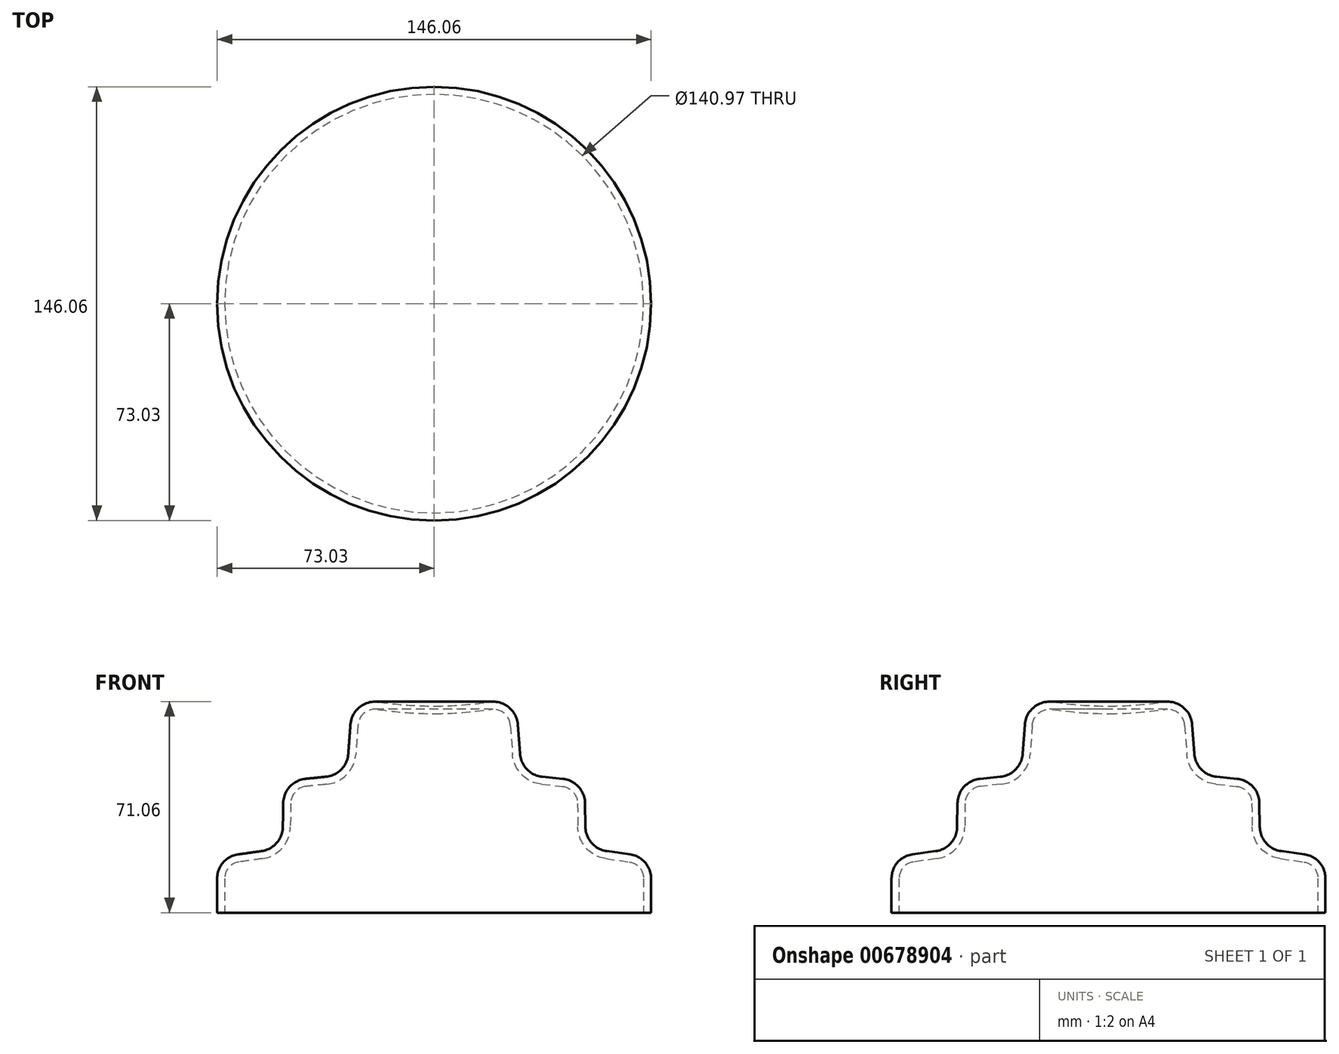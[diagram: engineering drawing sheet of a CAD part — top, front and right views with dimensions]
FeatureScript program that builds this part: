
annotation { "Feature Type Name" : "Feature", "Feature Type Description" : "" }
export const myFeature = defineFeature(function(context is Context, id is Id, definition is map)
    precondition{}
    {
        {
            var Q0;
            Q0=qCreatedBy(makeId("Front.planeOp"),FACE);
            var sketch = newSketch(context, id + "F0", { "sketchPlane" : qUnion([Q0])});
            skPoint(sketch, "E0.MirrorCS.end.orphan", {"position": v(0, -0.23) * mm});
            skLineSegment(sketch, "E1.MirrorCS", {"start": v(0, 66.8) * mm, "end": v(0, 69.34) * mm});
            skLineSegment(sketch, "E2.MirrorCS", {"start": v(73.03, -0.23) * mm, "end": v(73.03, 11.33) * mm});
            skLineSegment(sketch, "E3.MirrorCS", {"start": v(28.9, 53.28) * mm, "end": v(28.19, 63.05) * mm});
            skLineSegment(sketch, "E4.MirrorCS", {"start": v(50.92, 28.67) * mm, "end": v(50.8, 36.64) * mm});
            skPoint(sketch, "E5.MirrorP", {"position": v(50.51, 42.97) * mm});
            skArc(sketch, "E6.MirrorCS", {"start": v(58.13, 20.5) * mm, "mid": v(53.01, 23.25) * mm, "end": v(50.92, 28.67) * mm});
            skPoint(sketch, "E7.MirrorP", {"position": v(73.03, 18.38) * mm});
            skArc(sketch, "E8.MirrorCS", {"start": v(18.58, 70.74) * mm, "mid": v(9.31, 69.7) * mm, "end": v(0, 69.34) * mm});
            skPoint(sketch, "E9.MirrorP", {"position": v(43.25, 44.86) * mm});
            skArc(sketch, "E10.MirrorCS", {"start": v(43.25, 44.86) * mm, "mid": v(48.6, 42.19) * mm, "end": v(50.8, 36.64) * mm});
            skPoint(sketch, "E11.MirrorP", {"position": v(27.87, 71.34) * mm});
            skPoint(sketch, "E12.MirrorP", {"position": v(27.87, 44.06) * mm});
            skArc(sketch, "E13.MirrorCS", {"start": v(66.04, 19.37) * mm, "mid": v(71.03, 16.66) * mm, "end": v(73.03, 11.33) * mm});
            skArc(sketch, "E14.MirrorCS", {"start": v(18.58, 70.74) * mm, "mid": v(25.06, 69) * mm, "end": v(28.19, 63.05) * mm});
            skLineSegment(sketch, "E15.MirrorCS", {"start": v(58.13, 20.5) * mm, "end": v(66.04, 19.37) * mm});
            skArc(sketch, "E16.MirrorCS", {"start": v(36.42, 45.54) * mm, "mid": v(31.24, 48.03) * mm, "end": v(28.9, 53.28) * mm});
            skLineSegment(sketch, "E17.MirrorCS", {"start": v(0, -4.32) * mm, "end": v(0, 70.6) * mm});
            skLineSegment(sketch, "E18.MirrorCS", {"start": v(36.42, 45.54) * mm, "end": v(43.25, 44.86) * mm});
            skPoint(sketch, "E19.MirrorP", {"position": v(0, 69.34) * mm});
            skLineSegment(sketch, "E20", {"start": v(0, 0) * mm, "end": v(73.03, -0.23) * mm});
            skSolve(sketch);
        }
        {
            var Q0;
            Q0 = qSketchRegion(id + "F0", true);
            var Q1;
            Q1=sQuery(id+"F0.wireOp",EDGE,"E17.MirrorCS");
            revolve(context, id + "F1", {"surfaceOperationType" : NewSurfaceOperationType.NEW, "entities" : qUnion([Q0]), "axis" : qUnion([Q1]), "revolveType" : RevolveType.FULL});
        }
        {
            var Q0;
            Q0=makeQuery(id+"F1.opRevolve","SWEPT_FACE",FACE,{"disambiguationData":[OSD([sQuery(id+"F0.wireOp",EDGE,"E20")])]});
            shell(context, id + "F2", {"entities" : qUnion([Q0]), "thickness" : 2.54 * mm});
        }
    });
